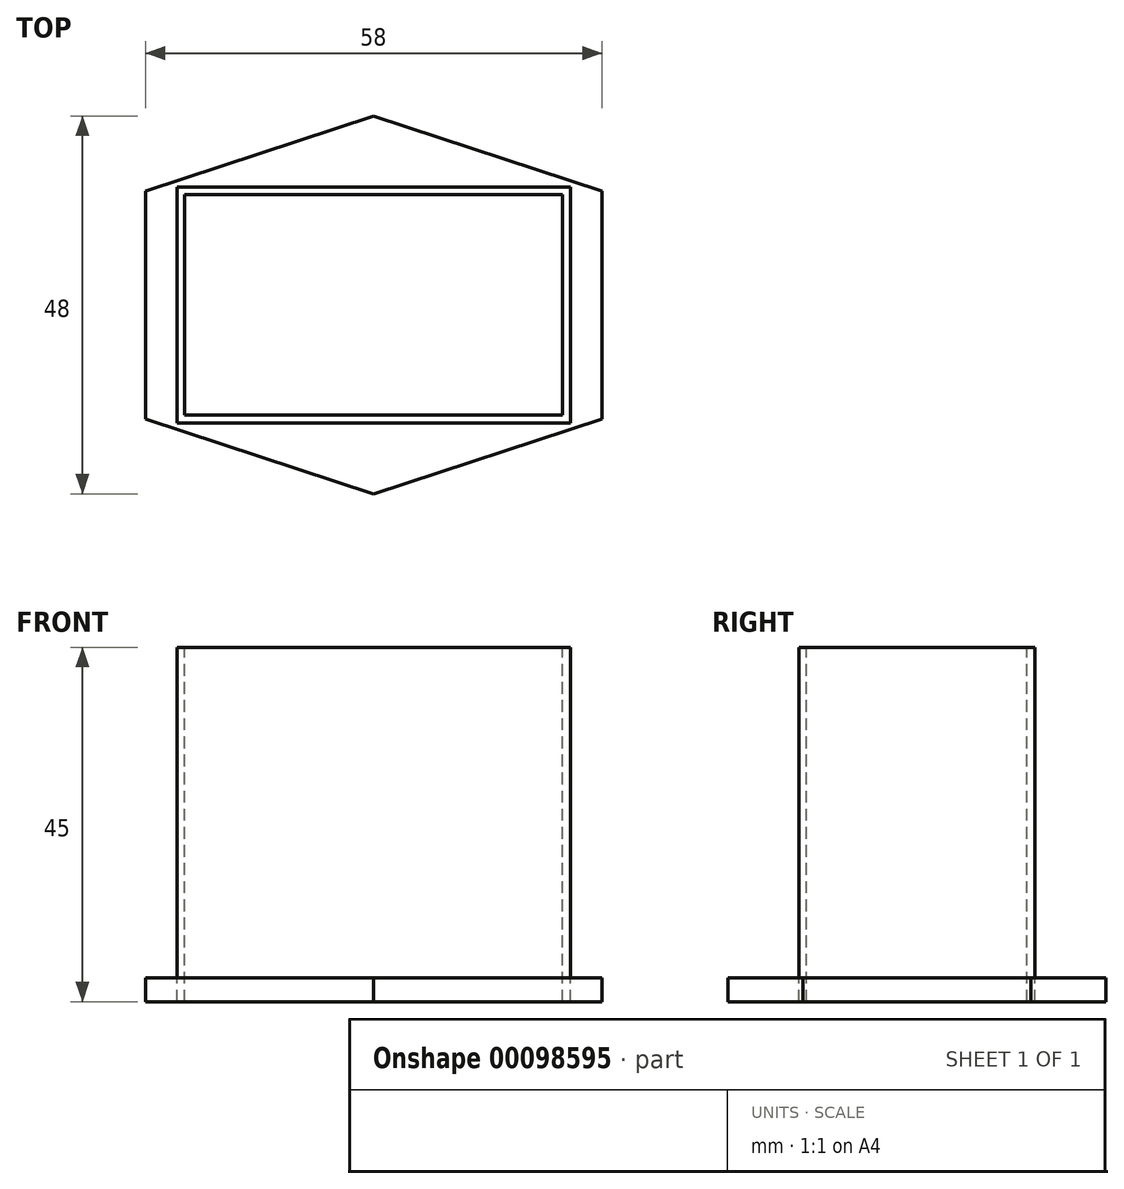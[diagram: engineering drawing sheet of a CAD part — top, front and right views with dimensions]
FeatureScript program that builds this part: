
annotation { "Feature Type Name" : "Feature", "Feature Type Description" : "" }
export const myFeature = defineFeature(function(context is Context, id is Id, definition is map)
    precondition{}
    {
        {
            var Q0;
            Q0=qCreatedBy(makeId("Top.planeOp"),FACE);
            var sketch = newSketch(context, id + "F0", { "sketchPlane" : qUnion([Q0])});
            skLineSegment(sketch, "E0", {"start": v(0, 24) * mm, "end": v(0, 0) * mm});
            skLineSegment(sketch, "E1", {"start": v(0, 0) * mm, "end": v(0, -24) * mm});
            skLineSegment(sketch, "E2", {"start": v(0, 0) * mm, "end": v(-29, 0) * mm});
            skLineSegment(sketch, "E3", {"start": v(-29, 0) * mm, "end": v(-29, 14.5) * mm});
            skLineSegment(sketch, "E4", {"start": v(-29, 0) * mm, "end": v(-29, -14.5) * mm});
            skLineSegment(sketch, "E5", {"start": v(0, 24) * mm, "end": v(-29, 14.5) * mm});
            skLineSegment(sketch, "E6", {"start": v(0, -24) * mm, "end": v(-29, -14.5) * mm});
            skLineSegment(sketch, "E7", {"start": v(-24, 0) * mm, "end": v(-24, 14) * mm});
            skLineSegment(sketch, "E8", {"start": v(-24, 14) * mm, "end": v(0, 14) * mm});
            skLineSegment(sketch, "E9.MirrorCS", {"start": v(-24, 0) * mm, "end": v(-24, -14) * mm});
            skLineSegment(sketch, "E10.MirrorCS", {"start": v(-24, -14) * mm, "end": v(0, -14) * mm});
            skLineSegment(sketch, "E11.MirrorCS", {"start": v(0, 24) * mm, "end": v(29, 14.5) * mm});
            skLineSegment(sketch, "E12.MirrorCS", {"start": v(29, 0) * mm, "end": v(29, 14.5) * mm});
            skLineSegment(sketch, "E13.MirrorCS", {"start": v(29, 0) * mm, "end": v(29, -14.5) * mm});
            skLineSegment(sketch, "E14.MirrorCS", {"start": v(0, -24) * mm, "end": v(29, -14.5) * mm});
            skLineSegment(sketch, "E15.MirrorCS", {"start": v(24, -14) * mm, "end": v(0, -14) * mm});
            skLineSegment(sketch, "E16.MirrorCS", {"start": v(24, 0) * mm, "end": v(24, -14) * mm});
            skLineSegment(sketch, "E17.MirrorCS", {"start": v(24, 0) * mm, "end": v(24, 14) * mm});
            skLineSegment(sketch, "E18.MirrorCS", {"start": v(24, 14) * mm, "end": v(0, 14) * mm});
            skLineSegment(sketch, "E19.0", {"start": v(-25, 0) * mm, "end": v(-25, 15) * mm});
            skLineSegment(sketch, "E19.1", {"start": v(-25, 0) * mm, "end": v(-25, -15) * mm});
            skLineSegment(sketch, "E19.2", {"start": v(-25, 15) * mm, "end": v(0, 15) * mm});
            skLineSegment(sketch, "E19.3", {"start": v(-25, -15) * mm, "end": v(0, -15) * mm});
            skLineSegment(sketch, "E19.4", {"start": v(25, 15) * mm, "end": v(0, 15) * mm});
            skLineSegment(sketch, "E19.5", {"start": v(25, 0) * mm, "end": v(25, 15) * mm});
            skLineSegment(sketch, "E19.6", {"start": v(25, 0) * mm, "end": v(25, -15) * mm});
            skLineSegment(sketch, "E19.7", {"start": v(25, -15) * mm, "end": v(0, -15) * mm});
            skCircle(sketch, "E20", {"center": v(0, -20) * mm, "radius": 1.5 * mm, "construction": true});
            skCircle(sketch, "E21.MirrorC", {"center": v(0, 20) * mm, "radius": 1.5 * mm, "construction": true});
            skSolve(sketch);
        }
        {
            var Q0;
            Q0=sQuery(id+"F0.wireOp",EDGE,"E6");
            var Q1;
            Q1=sQuery(id+"F0.wireOp",EDGE,"E4");
            var Q2;
            Q2=sQuery(id+"F0.wireOp",EDGE,"E3");
            var Q3;
            Q3=sQuery(id+"F0.wireOp",EDGE,"E5");
            var Q4;
            Q4=sQuery(id+"F0.wireOp",EDGE,"E11.MirrorCS");
            var Q5;
            Q5=sQuery(id+"F0.wireOp",EDGE,"E12.MirrorCS");
            var Q6;
            Q6=sQuery(id+"F0.wireOp",EDGE,"E13.MirrorCS");
            var Q7;
            Q7=sQuery(id+"F0.wireOp",EDGE,"E14.MirrorCS");
            var Q8;
            Q8=sQuery(id+"F0.wireOp",EDGE,"E19.6");
            var Q9;
            Q9=sQuery(id+"F0.wireOp",EDGE,"E19.7");
            var Q10;
            Q10=sQuery(id+"F0.wireOp",EDGE,"E19.3");
            var Q11;
            Q11=sQuery(id+"F0.wireOp",EDGE,"E19.1");
            var Q12;
            Q12=sQuery(id+"F0.wireOp",EDGE,"E19.0");
            var Q13;
            Q13=sQuery(id+"F0.wireOp",EDGE,"E19.2");
            var Q14;
            Q14=sQuery(id+"F0.wireOp",EDGE,"E19.4");
            var Q15;
            Q15=sQuery(id+"F0.wireOp",EDGE,"E19.5");
            extrude(context, id + "F1", {"bodyType" : ToolBodyType.SURFACE, "surfaceEntities" : qUnion([Q0, Q1, Q2, Q3, Q4, Q5, Q6, Q7, Q8, Q9, Q10, Q11, Q12, Q13, Q14, Q15]), "depth" : 3 * mm});
        }
        {
            var Q0;
            Q0=sQuery(id+"F0.wireOp",EDGE,"E19.3");
            var Q1;
            Q1=sQuery(id+"F0.wireOp",EDGE,"E10.MirrorCS");
            var Q2;
            Q2=sQuery(id+"F0.wireOp",EDGE,"E19.1");
            var Q3;
            Q3=sQuery(id+"F0.wireOp",EDGE,"E9.MirrorCS");
            var Q4;
            Q4=sQuery(id+"F0.wireOp",EDGE,"E19.0");
            var Q5;
            Q5=sQuery(id+"F0.wireOp",EDGE,"E7");
            var Q6;
            Q6=sQuery(id+"F0.wireOp",EDGE,"E8");
            var Q7;
            Q7=sQuery(id+"F0.wireOp",EDGE,"E19.2");
            var Q8;
            Q8=sQuery(id+"F0.wireOp",EDGE,"E19.4");
            var Q9;
            Q9=sQuery(id+"F0.wireOp",EDGE,"E18.MirrorCS");
            var Q10;
            Q10=sQuery(id+"F0.wireOp",EDGE,"E17.MirrorCS");
            var Q11;
            Q11=sQuery(id+"F0.wireOp",EDGE,"E19.5");
            var Q12;
            Q12=sQuery(id+"F0.wireOp",EDGE,"E19.6");
            var Q13;
            Q13=sQuery(id+"F0.wireOp",EDGE,"E16.MirrorCS");
            var Q14;
            Q14=sQuery(id+"F0.wireOp",EDGE,"E19.7");
            var Q15;
            Q15=sQuery(id+"F0.wireOp",EDGE,"E15.MirrorCS");
            extrude(context, id + "F2", {"bodyType" : ToolBodyType.SURFACE, "surfaceEntities" : qUnion([Q0, Q1, Q2, Q3, Q4, Q5, Q6, Q7, Q8, Q9, Q10, Q11, Q12, Q13, Q14, Q15]), "depth" : 45 * mm});
        }
    });
